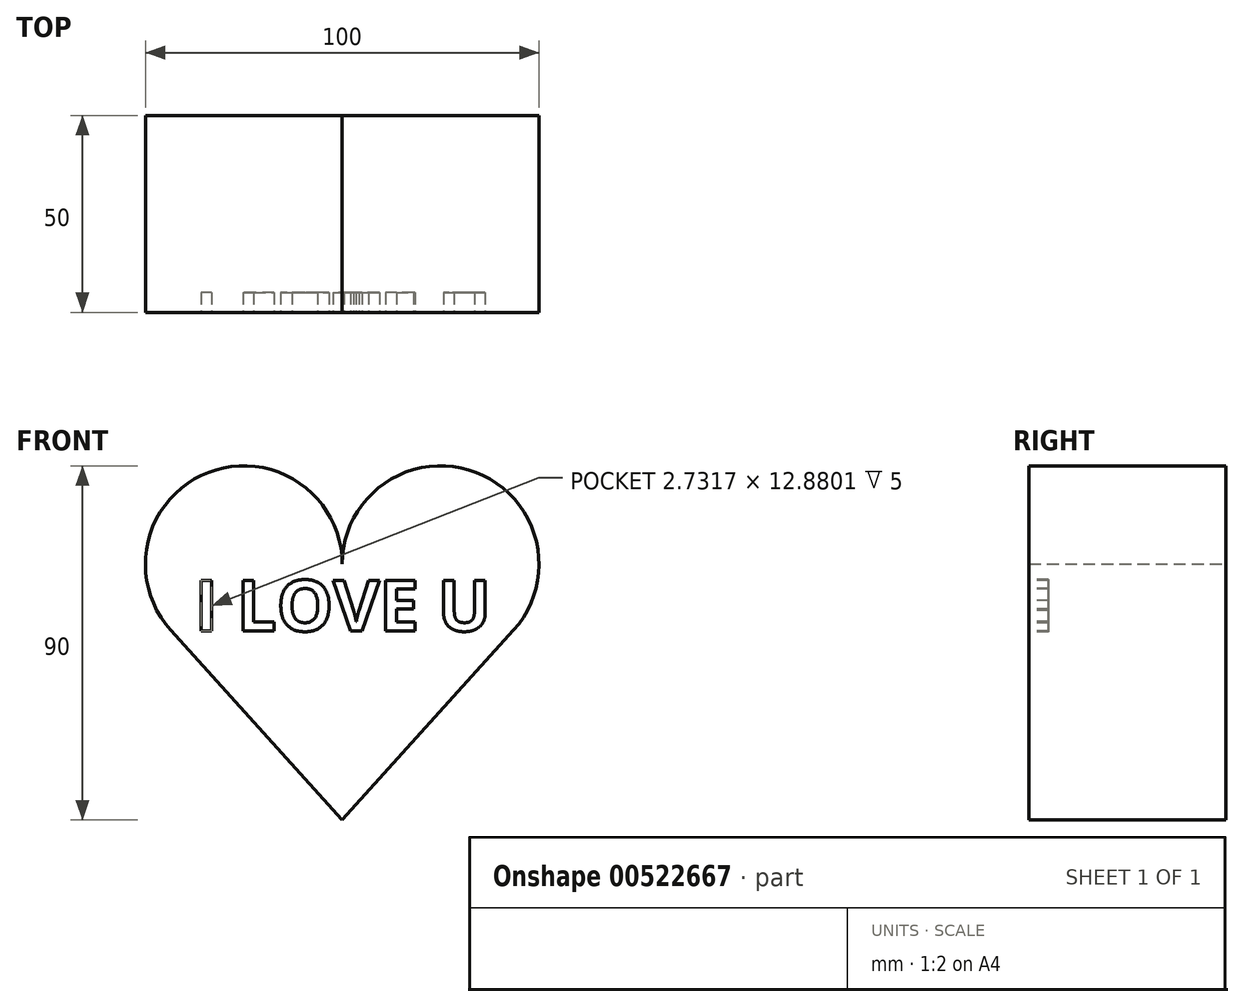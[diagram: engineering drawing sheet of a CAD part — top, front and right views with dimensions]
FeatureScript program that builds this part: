
annotation { "Feature Type Name" : "Feature", "Feature Type Description" : "" }
export const myFeature = defineFeature(function(context is Context, id is Id, definition is map)
    precondition{}
    {
        {
            var Q0;
            Q0=qCreatedBy(makeId("Front.planeOp"),FACE);
            var sketch = newSketch(context, id + "F0", { "sketchPlane" : qUnion([Q0])});
            skArc(sketch, "E0", {"start": v(0, 0) * mm, "mid": v(-33.97, 23.33) * mm, "end": v(-43.56, -16.75) * mm});
            skArc(sketch, "E1", {"start": v(43.56, -16.75) * mm, "mid": v(33.97, 23.33) * mm, "end": v(0, 0) * mm});
            skLineSegment(sketch, "E2", {"start": v(0, 0) * mm, "end": v(0, -65) * mm, "construction": true});
            skLineSegment(sketch, "E3", {"start": v(0, -65) * mm, "end": v(-43.56, -16.75) * mm});
            skLineSegment(sketch, "E4", {"start": v(0, -65) * mm, "end": v(43.56, -16.75) * mm});
            skPoint(sketch, "E5.orphan", {"position": v(-58.68, 0) * mm});
            skPoint(sketch, "E6.orphan", {"position": v(58.68, 0) * mm});
            skLineSegment(sketch, "E7", {"start": v(0, 0) * mm, "end": v(0, -65) * mm});
            skSolve(sketch);
        }
        {
            var Q0;
            Q0=makeQuery(id+"F0.imprint","IMPRINT",FACE,{"disambiguationData":[TD([[makeQuery(id+"F0.imprint","IMPRINT",EDGE,{"derivedFrom":sQuery(id+"F0.wireOp",EDGE,"E1")}),1.0]])]});
            var Q1;
            Q1=makeQuery(id+"F0.imprint","IMPRINT",FACE,{"disambiguationData":[TD([[makeQuery(id+"F0.imprint","IMPRINT",EDGE,{"derivedFrom":sQuery(id+"F0.wireOp",EDGE,"E0")}),1.0]])]});
            extrude(context, id + "F1", {"entities" : qUnion([Q0, Q1]), "depth" : 50 * mm, "offsetDistance" : 25 * mm});
        }
        {
            var Q0;
            Q0=makeQuery(id+"F1.opExtrude","CAP_FACE",FACE,{"disambiguationData":[OSD([sQuery(id+"F0.wireOp",EDGE,"E0"),sQuery(id+"F0.wireOp",EDGE,"E1"),sQuery(id+"F0.wireOp",EDGE,"E3"),sQuery(id+"F0.wireOp",EDGE,"E4")])],"isStart":false});
            var sketch = newSketch(context, id + "F2", { "sketchPlane" : qUnion([Q0])});
            skText(sketch, "E8", { "text": "I LOVE U", "fontName": "OpenSans-Bold.ttf"});
            const initialGuessF2  = {"E8": [-0.0375, -0.01699, 1, 0, 0.01299]};
            skSetInitialGuess(sketch, initialGuessF2);
            skSolve(sketch);
        }
        {
            var Q0;
            Q0 = qSketchRegion(id + "F2", true);
            extrude(context, id + "F3", {"entities" : qUnion([Q0]), "operationType" : NewBodyOperationType.REMOVE, "oppositeDirection" : true, "depth" : 5 * mm, "offsetDistance" : 25 * mm});
        }
    });
